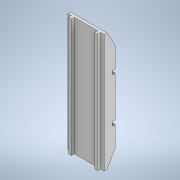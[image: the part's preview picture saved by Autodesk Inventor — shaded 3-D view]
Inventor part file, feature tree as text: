
AUTODESK INVENTOR PART (.ipt)
format: ipt  version: 2020 (Build 240168000, 168)  size: 138,240 bytes
history: native  units: in
note: dims shown in document units (in); Inventor stores cm internally (conversion verified against a paired STEP export)
features: extrude x3, sketch x3, chamfer x2
ambient origin geometry x8: Origin, YZ Plane, XZ Plane, XY Plane, X Axis, Y Axis, Z Axis, Center Point
bodies: Solid1 (feature_tree)
feature tree (8):
  extrude  "Extrusion1"  Depth=2.3622in
  chamfer  "Chamfer1"  Distance=25.5906in
  chamfer  "Chamfer2"  Distance=1.7717in Angle=45.0deg
  extrude  "Extrusion2"  Depth=0.7874in
  extrude  "Extrusion3"  Depth=0.6299in
  sketch  "Sketch1"  dims[d0=7.874in d1=2.3622in]
  sketch  "Sketch2"  dims[d2=7.6772in d3=25.5906in d4=0.0in d5=1.7717in d6=3.1496in d7=45.0deg]
  sketch  "Sketch3"  dims[d8=1.7717in d9=3.1496in d10=45.0deg d11=0.7874in d12=0.6299in d13=0.6299in d14=25.5906in d15=0.0in d16=8.8189in d17=0.6299in d18=0.7874in d19=0.0in d20=0.0in]
